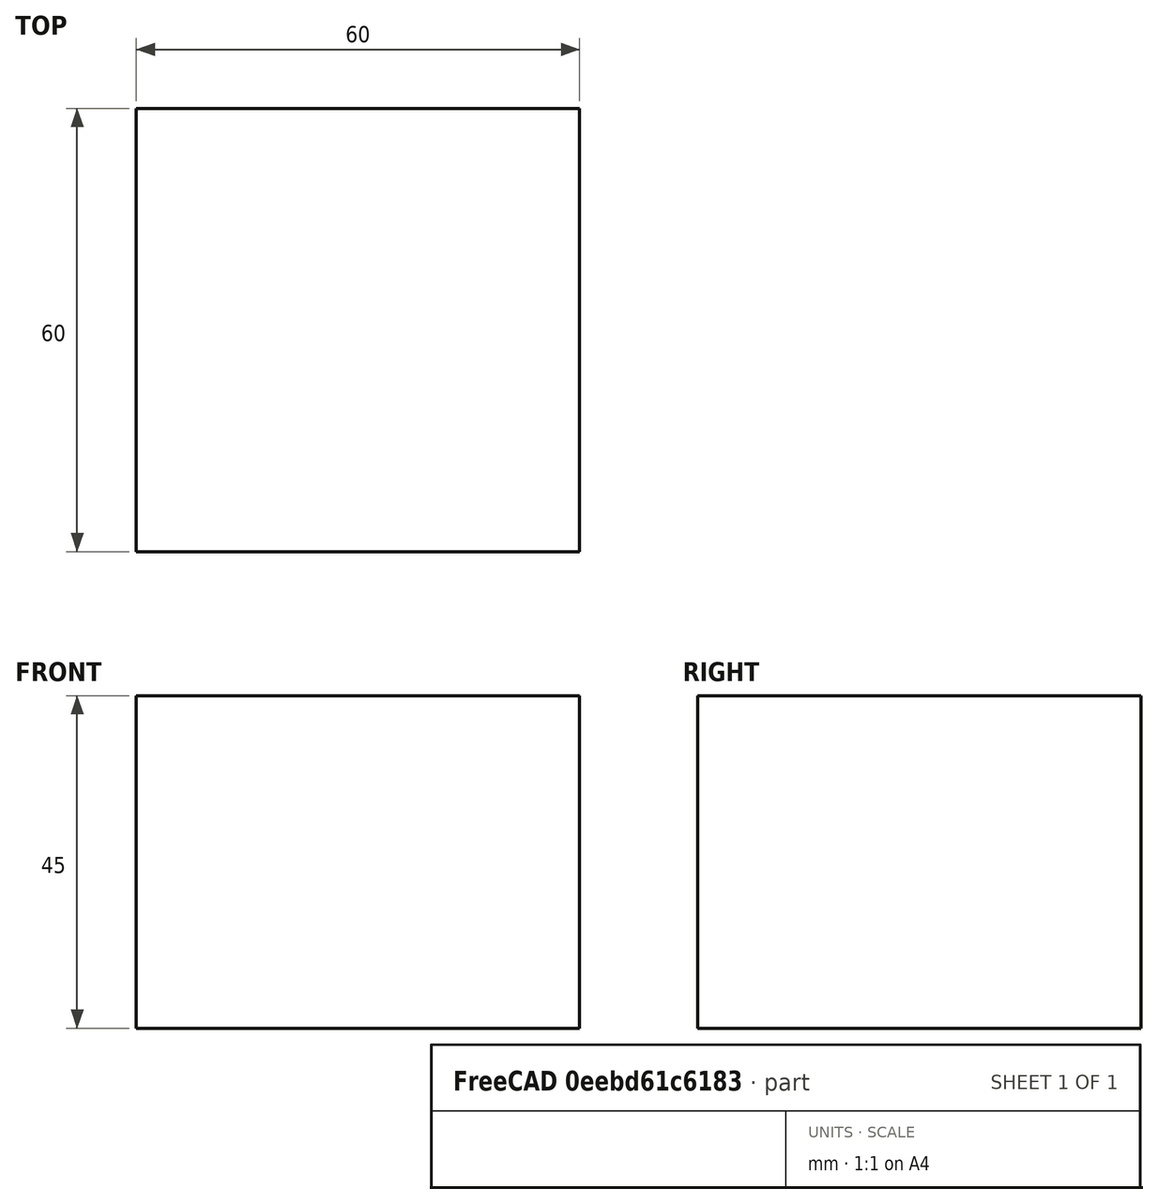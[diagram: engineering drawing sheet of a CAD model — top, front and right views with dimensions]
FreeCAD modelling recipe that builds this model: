
FCSTD DOCUMENT  (FreeCAD 0.18R16110 (Git))
Label: cad2(1)
License: All rights reserved
LicenseURL: http://en.wikipedia.org/wiki/All_rights_reserved
objects: Part::Box×1, Sketcher::SketchObject×1
note: 2 computed .brp shape members not serialized (recipe doc carries the construction recipe); baked Part::Feature solids carry a one-line shape summary decoded from their .brp

FEATURE [Part::Box] Box  label="Cubo"
  AttacherType = Attacher::AttachEngine3D
  Height = 45
  Length = 60
  Width = 60
FEATURE [Sketcher::SketchObject] Sketch
  MapMode = 5
  Placement = pos=(0,0,45) rot=(0,0,1;0rad)
  sketch-geometry (27):
    g0: LineSegment StartX=5 StartY=55 StartZ=0 EndX=55 EndY=55 EndZ=0
    g1: LineSegment StartX=5 StartY=5 StartZ=0 EndX=55 EndY=5 EndZ=0
    g2: LineSegment StartX=5 StartY=55 StartZ=0 EndX=5 EndY=37.5 EndZ=0
    g3: LineSegment StartX=5 StartY=5 StartZ=0 EndX=5 EndY=22.5 EndZ=0
    g4: LineSegment StartX=5 StartY=22.5 StartZ=0 EndX=10 EndY=22.5 EndZ=0
    g5: LineSegment StartX=10 StartY=37.5 StartZ=0 EndX=5 EndY=37.5 EndZ=0
    g6: LineSegment StartX=55 StartY=55 StartZ=0 EndX=55 EndY=37.5 EndZ=0
    g7: LineSegment StartX=55 StartY=5 StartZ=0 EndX=55 EndY=22.5 EndZ=0
    g8: LineSegment StartX=55 StartY=37.5 StartZ=0 EndX=50 EndY=37.5 EndZ=0
    g9: LineSegment StartX=50 StartY=22.5 StartZ=0 EndX=55 EndY=22.5 EndZ=0
    g10: GeomPoint [constr] X=60 Y=0 Z=0
    g11: GeomPoint [constr] X=60 Y=60 Z=0
    g12: GeomPoint [constr] X=0 Y=60 Z=0
    g13: LineSegment StartX=50.001 StartY=37.5 StartZ=0 EndX=45 EndY=37.5 EndZ=0
    g14: LineSegment StartX=45 StartY=37.5 StartZ=0 EndX=45 EndY=32.5 EndZ=0
    g15: LineSegment StartX=45 StartY=32.5 StartZ=0 EndX=50 EndY=32.5 EndZ=0
    g16: LineSegment StartX=50 StartY=27.5 StartZ=0 EndX=45 EndY=27.5 EndZ=0
    g17: LineSegment StartX=45 StartY=27.5 StartZ=0 EndX=45 EndY=22.5 EndZ=0
    g18: LineSegment StartX=45 StartY=22.5 StartZ=0 EndX=50.0094 EndY=22.4998 EndZ=0
    g19: LineSegment StartX=50 StartY=32.5 StartZ=0 EndX=50 EndY=27.5 EndZ=0
    g20: LineSegment StartX=10 StartY=37.5 StartZ=0 EndX=15 EndY=37.5 EndZ=0
    g21: LineSegment StartX=15 StartY=37.5 StartZ=0 EndX=15 EndY=32.5 EndZ=0
    g22: LineSegment StartX=15 StartY=32.5 StartZ=0 EndX=10 EndY=32.5 EndZ=0
    g23: LineSegment StartX=10 StartY=32.4939 StartZ=0 EndX=10 EndY=27.5 EndZ=0
    g24: LineSegment StartX=10 StartY=27.5 StartZ=0 EndX=15 EndY=27.5 EndZ=0
    g25: LineSegment StartX=15 StartY=27.5 StartZ=0 EndX=15 EndY=22.5 EndZ=0
    g26: LineSegment StartX=15 StartY=22.5 StartZ=0 EndX=10 EndY=22.5 EndZ=0
  constraints (76):
    c: DistanceY(g2,g0) = 17.5
    c: DistanceY(g5,g0) = 17.5
    c: DistanceX(g5,g2) = -5
    c: DistanceX(g4,g3) = -5
    c: DistanceY(g3,g1) = -17.5
    c: DistanceY(g2,g1) = -50
    c: DistanceY(g3,g0) = 50
    c: DistanceX(g1,g1) = 50
    c: DistanceY(g-1,g1) = 5
    c: DistanceX(g-1,g3) = 5
    c: DistanceY(g-1,g7) = 5
    c: DistanceY(g1,g0) = 50
    c: DistanceY(g1,g6) = 50
    c: DistanceX(g6,g8) = -5
    c: DistanceX(g9,g7) = 5
    c: DistanceY(g7,g1) = -17.5
    c: DistanceY(g8,g0) = 17.5
    c: DistanceX(g0,g0) = 50
    c: DistanceX(g1,g7) = 50
    c: DistanceX(g-1,g1) = 5
    c: DistanceX(g-1,g0) = 5
    c: DistanceY(g1,g10) = -5
    c: DistanceX(g6,g11) = 5
    c: DistanceX(g8,g11) = 5
    c: DistanceX(g9,g11) = 10
    c: DistanceX(g9,g10) = 5
    c: DistanceX(g6,g11) = 5
    c: DistanceX(g8,g5) = -40
    c: DistanceX(g12,g2) = 5
    c: DistanceY(g12,g0) = -5
    c: Coincident(g13,g14)
    c: Coincident(g14,g15)
    c: DistanceY(g13,g15) = -5
    c: DistanceY(g13,g14) = -5
    c: DistanceY(g8,g14) = -5
    c: DistanceY(g15,g8) = 5
    c: DistanceX(g6,g14) = -10
    c: Coincident(g16,g17)
    c: Coincident(g17,g18)
    c: DistanceX(g16,g16) = 5
    c: DistanceY(g16,g17) = -5
    c: DistanceY(g16,g9) = -5
    c: DistanceX(g15,g14) = -5
    c: DistanceX(g19,g16) = -5
    c: DistanceY(g19,g15) = 5
    c: DistanceY(g16,g15) = 5
    c: DistanceY(g19,g16) = -5
    c: DistanceY(g19,g16) = -5
    c: DistanceX(g16,g19) = 5
    c: DistanceX(g17,g7) = 10
    c: DistanceY(g7,g16) = 5
    c: Coincident(g20,g21)
    c: Coincident(g21,g22)
    c: Coincident(g23,g24)
    c: Coincident(g24,g25)
    c: Coincident(g25,g26)
    c: DistanceX(g25,g4) = -5
    c: DistanceX(g24,g23) = -5
    c: DistanceX(g26,g3) = -5
    c: DistanceY(g4,g24) = 5
    c: DistanceY(g26,g24) = 5
    c: DistanceY(g3,g24) = 5
    c: DistanceX(g4,g25) = 10
    c: DistanceY(g23,g25) = -5
    c: DistanceY(g23,g4) = -5
    c: DistanceX(g24,g4) = -5
    c: DistanceY(g24,g22) = 5
    c: DistanceX(g22,g24) = 5
    c: DistanceX(g23,g21) = 5
    c: DistanceY(g23,g21) = 5
    c: DistanceX(g21,g23) = -5
    c: DistanceY(g21,g20) = 5
    c: DistanceX(g22,g20) = 5
    c: DistanceX(g20,g5) = -5
    c: DistanceX(g2,g5) = 0
    c: DistanceY(g14,g6) = 5
